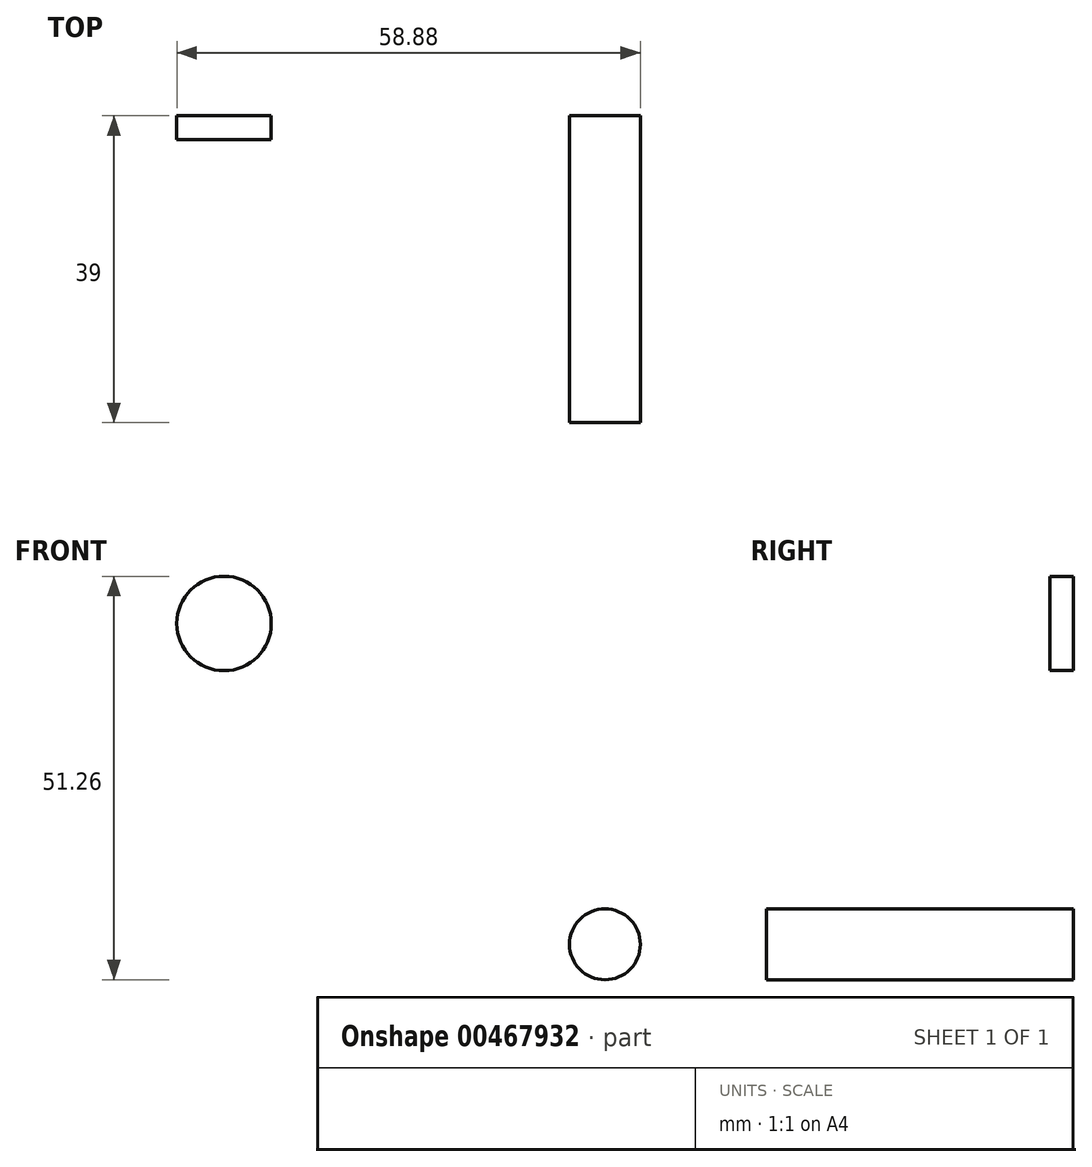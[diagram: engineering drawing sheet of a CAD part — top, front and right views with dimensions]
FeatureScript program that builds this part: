
annotation { "Feature Type Name" : "Feature", "Feature Type Description" : "" }
export const myFeature = defineFeature(function(context is Context, id is Id, definition is map)
    precondition{}
    {
        {
            var Q0;
            Q0=qCreatedBy(makeId("Front.planeOp"),FACE);
            var sketch = newSketch(context, id + "F0", { "sketchPlane" : qUnion([Q0])});
            skCircle(sketch, "E0", {"center": v(0, 0) * mm, "radius": 4.5 * mm});
            skPoint(sketch, "E1", {"position": v(-4.5, 0) * mm});
            skPoint(sketch, "E2", {"position": v(4.5, 0) * mm});
            skLineSegment(sketch, "E3", {"start": v(-4.5, 0) * mm, "end": v(4.5, 0) * mm});
            skSolve(sketch);
        }
        {
            var Q0;
            {var subQ0=sQuery(id+"F0.wireOp",EDGE,"E3");Q0=makeQuery(id+"F0.imprint","IMPRINT",FACE,{"disambiguationData":[TD([[makeQuery(id+"F0.imprint","IMPRINT",EDGE,{"derivedFrom":subQ0}),1.0]])]});}
            var Q1;
            {var subQ0=sQuery(id+"F0.wireOp",EDGE,"E3");Q1=makeQuery(id+"F0.imprint","IMPRINT",FACE,{"disambiguationData":[TD([[makeQuery(id+"F0.imprint","IMPRINT",EDGE,{"derivedFrom":subQ0}),-1.0]])]});}
            extrude(context, id + "F1", {"entities" : qUnion([Q0, Q1]), "depth" : 39 * mm});
        }
        {
            var Q0;
            Q0=qCreatedBy(makeId("Front.planeOp"),FACE);
            var sketch = newSketch(context, id + "F2", { "sketchPlane" : qUnion([Q0])});
            skCircle(sketch, "E4", {"center": v(-48.38, 40.76) * mm, "radius": 6 * mm});
            skLineSegment(sketch, "E5", {"start": v(-48.38, 40.76) * mm, "end": v(-54.18, 42.3) * mm});
            skLineSegment(sketch, "E6", {"start": v(-54.18, 42.3) * mm, "end": v(-42.58, 39.22) * mm});
            skSolve(sketch);
        }
        {
            var Q0;
            Q0 = qSketchRegion(id + "F2", true);
            extrude(context, id + "F3", {"entities" : qUnion([Q0]), "depth" : 3 * mm});
        }
    });
